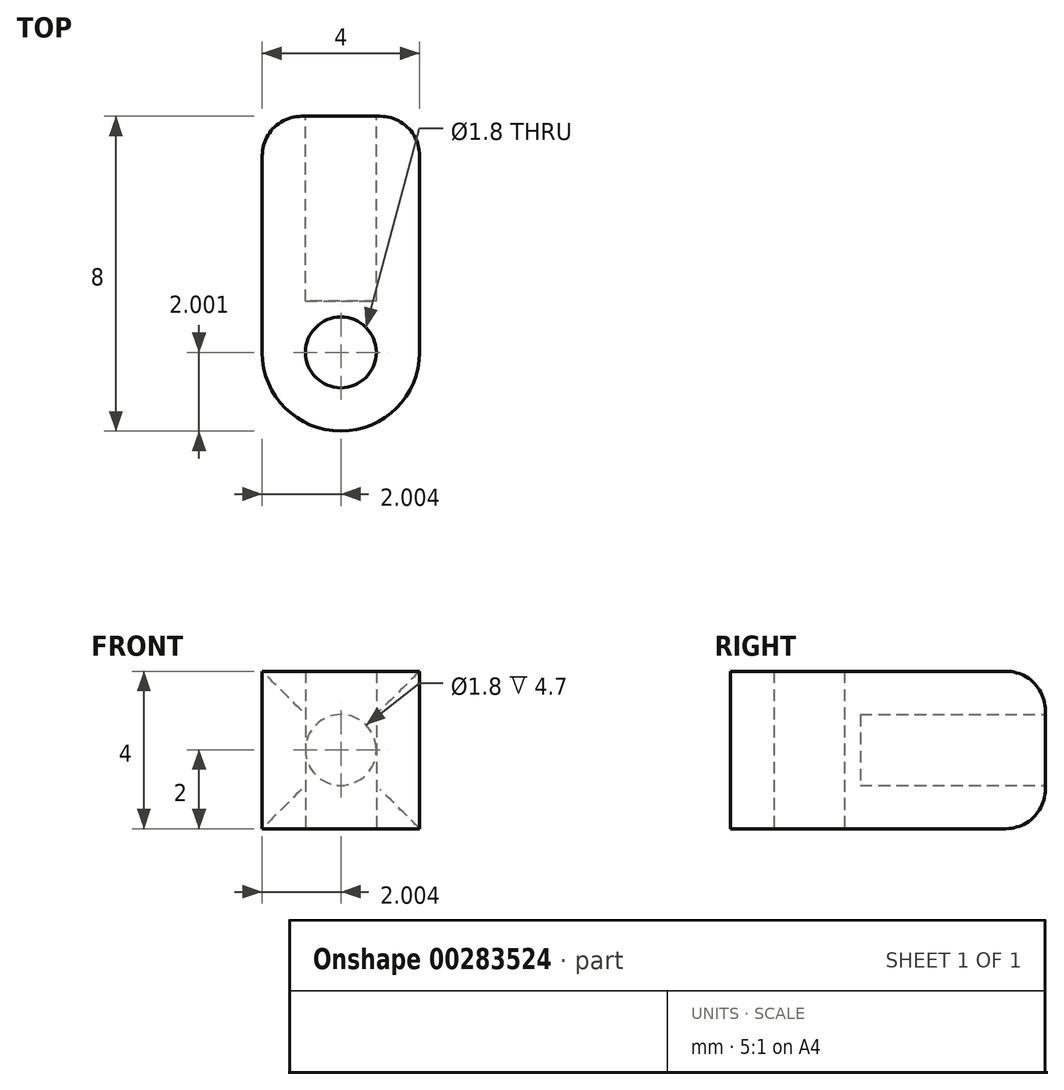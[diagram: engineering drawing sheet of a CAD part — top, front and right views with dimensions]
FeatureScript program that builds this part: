
annotation { "Feature Type Name" : "Feature", "Feature Type Description" : "" }
export const myFeature = defineFeature(function(context is Context, id is Id, definition is map)
    precondition{}
    {
        {
            var Q0;
            Q0=qCreatedBy(makeId("Top.planeOp"),FACE);
            var sketch = newSketch(context, id + "F0", { "sketchPlane" : qUnion([Q0])});
            skCircle(sketch, "E0", {"center": v(-134.6, -70.35) * mm, "radius": 0.9 * mm});
            skArc(sketch, "E1", {"start": v(-136.6, -70.35) * mm, "mid": v(-134.6, -72.35) * mm, "end": v(-132.6, -70.35) * mm});
            skLineSegment(sketch, "E2", {"start": v(-136.6, -70.35) * mm, "end": v(-136.6, -64.35) * mm});
            skLineSegment(sketch, "E3", {"start": v(-132.6, -64.35) * mm, "end": v(-136.6, -64.35) * mm});
            skLineSegment(sketch, "E4", {"start": v(-132.6, -64.35) * mm, "end": v(-132.6, -70.35) * mm});
            skSolve(sketch);
        }
        {
            var Q0;
            Q0=makeQuery(id+"F0.imprint","IMPRINT",FACE,{"disambiguationData":[TD([[makeQuery(id+"F0.imprint","IMPRINT",EDGE,{"derivedFrom":sQuery(id+"F0.wireOp",EDGE,"E0")}),-1.0]])]});
            extrude(context, id + "F1", {"entities" : qUnion([Q0]), "depth" : 4 * mm});
        }
        {
            var Q0;
            Q0=makeQuery(id+"F1.opExtrude","SWEPT_FACE",FACE,{"disambiguationData":[OSD([sQuery(id+"F0.wireOp",EDGE,"E3")])]});
            var sketch = newSketch(context, id + "F2", { "sketchPlane" : qUnion([Q0])});
            skLineSegment(sketch, "E5", {"start": v(136.6, 2) * mm, "end": v(132.6, 2) * mm, "construction": true});
            skCircle(sketch, "E6", {"center": v(134.6, 2) * mm, "radius": 0.9 * mm});
            skSolve(sketch);
        }
        {
            var Q0;
            Q0=makeQuery(id+"F2.imprint","IMPRINT",FACE,{"disambiguationData":[TD([[makeQuery(id+"F2.imprint","IMPRINT",EDGE,{"derivedFrom":sQuery(id+"F2.wireOp",EDGE,"E6")}),1.0]])]});
            extrude(context, id + "F3", {"entities" : qUnion([Q0]), "operationType" : NewBodyOperationType.REMOVE, "oppositeDirection" : true, "depth" : 4.7 * mm});
        }
        {
            var Q0;
            Q0=makeQuery(id+"F1.opExtrude","SWEPT_EDGE",EDGE,{"disambiguationData":[OSD([sQuery(id+"F0.wireOp",EDGE,"E3"),sQuery(id+"F0.wireOp",EDGE,"E4")])]});
            var Q1;
            Q1=makeQuery(id+"F1.opExtrude","CAP_EDGE",EDGE,{"disambiguationData":[OSD([sQuery(id+"F0.wireOp",EDGE,"E3")])],"isStart":true});
            var Q2;
            Q2=makeQuery(id+"F1.opExtrude","SWEPT_EDGE",EDGE,{"disambiguationData":[OSD([sQuery(id+"F0.wireOp",EDGE,"E2"),sQuery(id+"F0.wireOp",EDGE,"E3")])]});
            var Q3;
            Q3=makeQuery(id+"F1.opExtrude","CAP_EDGE",EDGE,{"disambiguationData":[OSD([sQuery(id+"F0.wireOp",EDGE,"E3")])],"isStart":false});
            fillet(context, id + "F4", {"entities" : qUnion([Q0, Q1, Q2, Q3]), "radius" : 1 * mm, "tangentPropagation" : true, "allowEdgeOverflow" : false});
        }
    });
